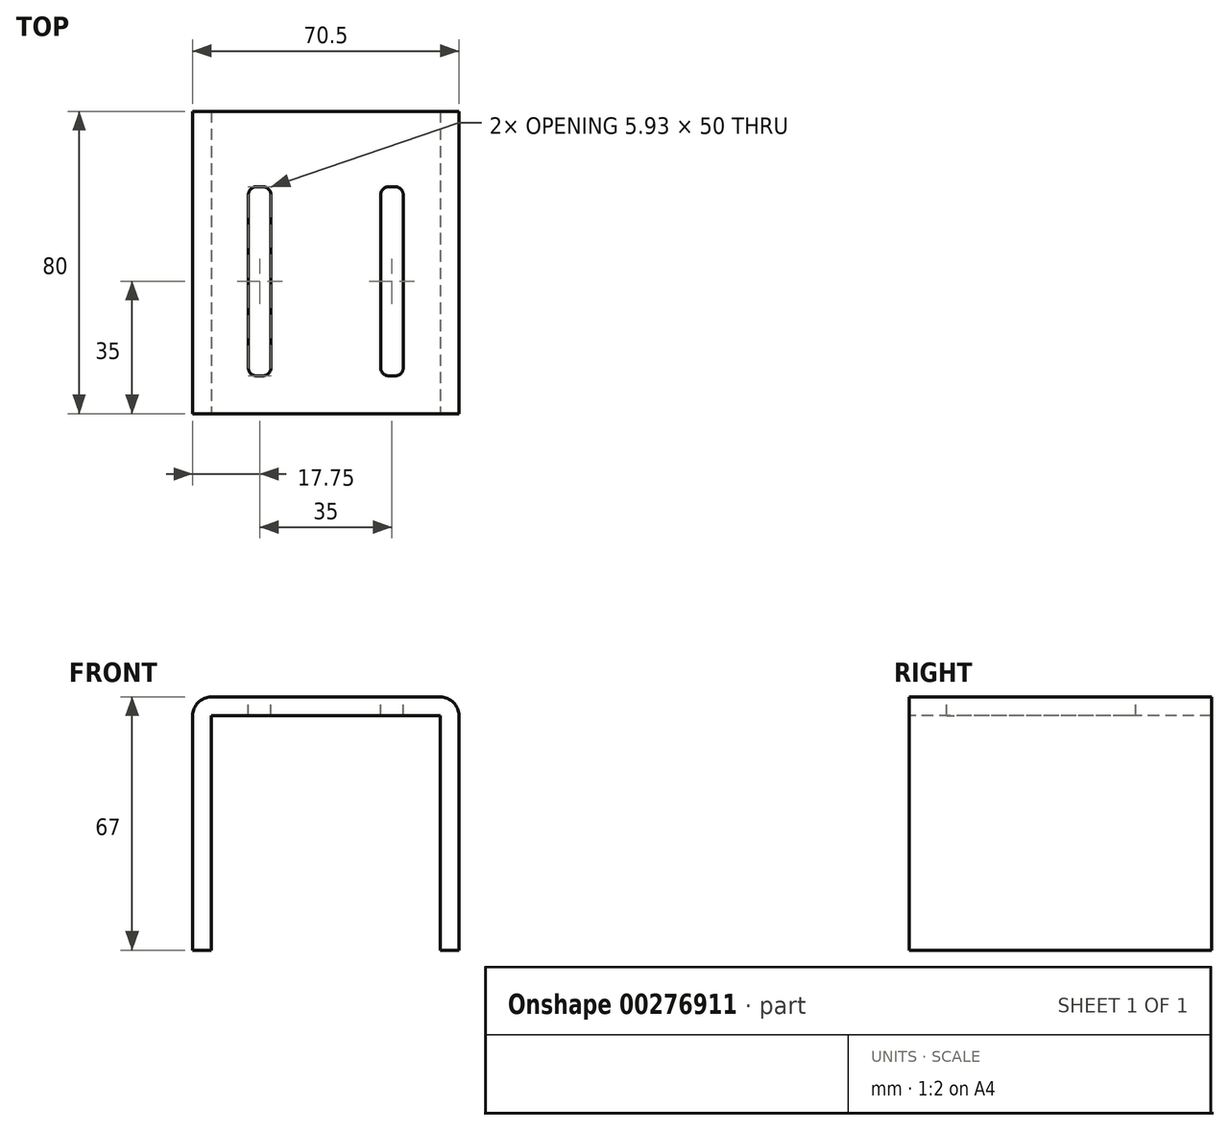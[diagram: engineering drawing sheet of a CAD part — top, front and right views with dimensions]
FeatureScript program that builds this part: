
annotation { "Feature Type Name" : "Feature", "Feature Type Description" : "" }
export const myFeature = defineFeature(function(context is Context, id is Id, definition is map)
    precondition{}
    {
        {
            var Q0;
            Q0=qCreatedBy(makeId("Front.planeOp"),FACE);
            var sketch = newSketch(context, id + "F0", { "sketchPlane" : qUnion([Q0])});
            skLineSegment(sketch, "E0", {"start": v(0, -50.14) * mm, "end": v(0, 57.83) * mm, "construction": true});
            skLineSegment(sketch, "E1", {"start": v(-35.25, 0) * mm, "end": v(-35.25, 62) * mm});
            skLineSegment(sketch, "E2", {"start": v(-30.25, 67) * mm, "end": v(30.25, 67) * mm});
            skLineSegment(sketch, "E3", {"start": v(35.25, 62) * mm, "end": v(35.25, 0) * mm});
            skLineSegment(sketch, "E4", {"start": v(-30.25, 0) * mm, "end": v(-30.25, 62) * mm});
            skLineSegment(sketch, "E5", {"start": v(-30.25, 62) * mm, "end": v(30.25, 62) * mm});
            skLineSegment(sketch, "E6", {"start": v(30.25, 62) * mm, "end": v(30.25, 0) * mm});
            skLineSegment(sketch, "E7", {"start": v(30.25, 0) * mm, "end": v(35.25, 0) * mm});
            skLineSegment(sketch, "E8", {"start": v(-30.25, 0) * mm, "end": v(-35.25, 0) * mm});
            skPoint(sketch, "E9.visualSharp", {"position": v(-35.25, 67) * mm});
            skArc(sketch, "E9.filletArc", {"start": v(-30.25, 67) * mm, "mid": v(-33.79, 65.54) * mm, "end": v(-35.25, 62) * mm});
            skPoint(sketch, "E10.visualSharp", {"position": v(35.25, 67) * mm});
            skArc(sketch, "E10.filletArc", {"start": v(35.25, 62) * mm, "mid": v(33.79, 65.54) * mm, "end": v(30.25, 67) * mm});
            skSolve(sketch);
        }
        {
            var Q0;
            Q0=makeQuery(id+"F0.imprint","IMPRINT",FACE,{"disambiguationData":[TD([[makeQuery(id+"F0.imprint","IMPRINT",EDGE,{"derivedFrom":sQuery(id+"F0.wireOp",EDGE,"E1")}),-1.0]])]});
            extrude(context, id + "F1", {"entities" : qUnion([Q0]), "oppositeDirection" : true, "depth" : 80 * mm});
        }
        {
            var Q0;
            Q0=makeQuery(id+"F1.opExtrude","SWEPT_FACE",FACE,{"disambiguationData":[OSD([sQuery(id+"F0.wireOp",EDGE,"E2")])]});
            var sketch = newSketch(context, id + "F2", { "sketchPlane" : qUnion([Q0])});
            skLineSegment(sketch, "E11", {"start": v(0, 0) * mm, "end": v(0, 80) * mm, "construction": true});
            skLineSegment(sketch, "E12", {"start": v(17.5, 80) * mm, "end": v(17.5, 0) * mm, "construction": true});
            skLineSegment(sketch, "E13", {"start": v(-17.5, 80) * mm, "end": v(-17.5, 0) * mm, "construction": true});
            skLineSegment(sketch, "E14.bottom", {"start": v(18.47, 10) * mm, "end": v(16.53, 10) * mm});
            skLineSegment(sketch, "E14.top", {"start": v(18.47, 60) * mm, "end": v(16.53, 60) * mm});
            skLineSegment(sketch, "E14.left", {"start": v(20.47, 12) * mm, "end": v(20.47, 58) * mm});
            skLineSegment(sketch, "E14.right", {"start": v(14.53, 12) * mm, "end": v(14.53, 58) * mm});
            skLineSegment(sketch, "E15.bottom", {"start": v(-16.53, 10) * mm, "end": v(-18.47, 10) * mm});
            skLineSegment(sketch, "E15.top", {"start": v(-16.53, 60) * mm, "end": v(-18.47, 60) * mm});
            skLineSegment(sketch, "E15.left", {"start": v(-14.53, 12) * mm, "end": v(-14.53, 58) * mm});
            skLineSegment(sketch, "E15.right", {"start": v(-20.47, 12) * mm, "end": v(-20.47, 58) * mm});
            skPoint(sketch, "E16.visualSharp", {"position": v(20.47, 10) * mm});
            skArc(sketch, "E16.filletArc", {"start": v(18.47, 10) * mm, "mid": v(19.88, 10.59) * mm, "end": v(20.47, 12) * mm});
            skPoint(sketch, "E17.visualSharp", {"position": v(14.53, 10) * mm});
            skArc(sketch, "E17.filletArc", {"start": v(14.53, 12) * mm, "mid": v(15.12, 10.59) * mm, "end": v(16.53, 10) * mm});
            skPoint(sketch, "E18.visualSharp", {"position": v(14.53, 60) * mm});
            skArc(sketch, "E18.filletArc", {"start": v(16.53, 60) * mm, "mid": v(15.12, 59.41) * mm, "end": v(14.53, 58) * mm});
            skPoint(sketch, "E19.visualSharp", {"position": v(20.47, 60) * mm});
            skArc(sketch, "E19.filletArc", {"start": v(20.47, 58) * mm, "mid": v(19.88, 59.41) * mm, "end": v(18.47, 60) * mm});
            skPoint(sketch, "E20.visualSharp", {"position": v(-14.53, 60) * mm});
            skArc(sketch, "E20.filletArc", {"start": v(-14.53, 58) * mm, "mid": v(-15.12, 59.41) * mm, "end": v(-16.53, 60) * mm});
            skPoint(sketch, "E21.visualSharp", {"position": v(-20.47, 60) * mm});
            skArc(sketch, "E21.filletArc", {"start": v(-18.47, 60) * mm, "mid": v(-19.88, 59.41) * mm, "end": v(-20.47, 58) * mm});
            skPoint(sketch, "E22.visualSharp", {"position": v(-14.53, 10) * mm});
            skArc(sketch, "E22.filletArc", {"start": v(-16.53, 10) * mm, "mid": v(-15.12, 10.59) * mm, "end": v(-14.53, 12) * mm});
            skPoint(sketch, "E23.visualSharp", {"position": v(-20.47, 10) * mm});
            skArc(sketch, "E23.filletArc", {"start": v(-20.47, 12) * mm, "mid": v(-19.88, 10.59) * mm, "end": v(-18.47, 10) * mm});
            skSolve(sketch);
        }
        {
            var Q0;
            Q0=makeQuery(id+"F2.imprint","IMPRINT",FACE,{"disambiguationData":[TD([[makeQuery(id+"F2.imprint","IMPRINT",EDGE,{"derivedFrom":sQuery(id+"F2.wireOp",EDGE,"E14.bottom")}),-1.0]])]});
            var Q1;
            Q1=makeQuery(id+"F2.imprint","IMPRINT",FACE,{"disambiguationData":[TD([[makeQuery(id+"F2.imprint","IMPRINT",EDGE,{"derivedFrom":sQuery(id+"F2.wireOp",EDGE,"E15.bottom")}),-1.0]])]});
            extrude(context, id + "F3", {"entities" : qUnion([Q0, Q1]), "operationType" : NewBodyOperationType.REMOVE, "endBound" : BoundingType.THROUGH_ALL, "oppositeDirection" : true, "depth" : 25 * mm});
        }
    });
